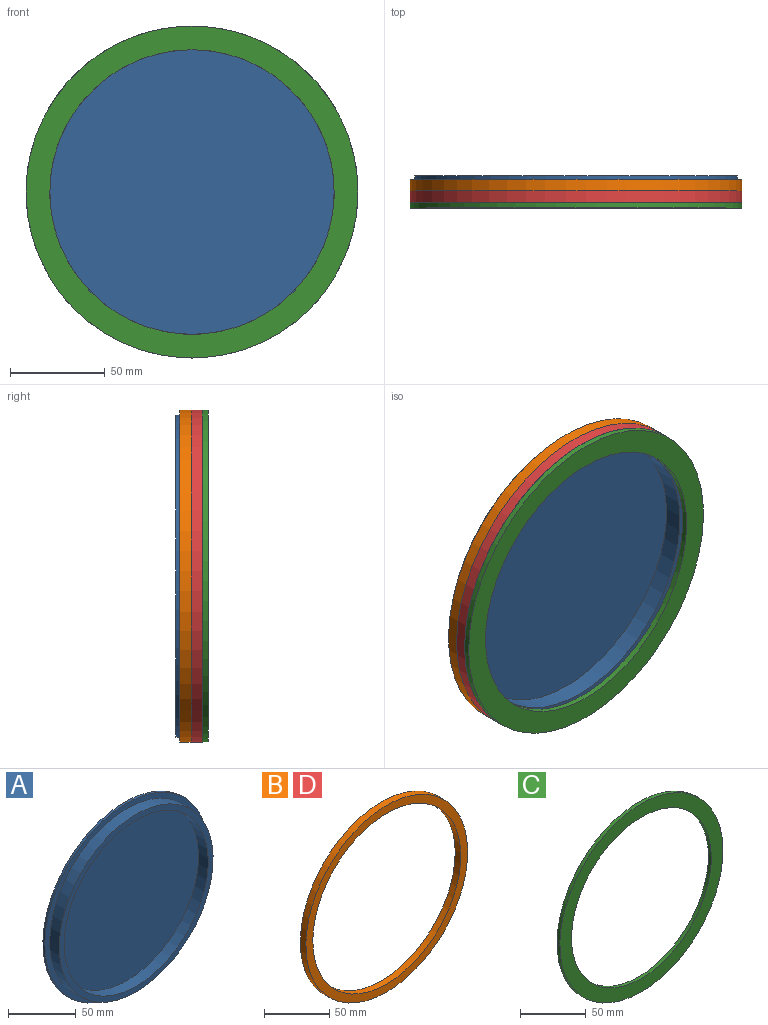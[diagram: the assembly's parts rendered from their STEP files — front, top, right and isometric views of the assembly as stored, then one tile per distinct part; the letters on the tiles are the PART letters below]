
ASSEMBLY  parts=4 mates=3
PART A: 7 faces, bbox 170x12x170 mm
  f0: cylinder r=75mm len=150mm, axis (0,1,0), area 4712.4mm2, adj f2,f6
  f1: cylinder r=80mm len=160mm, axis (0,1,0), area 5026.5mm2, adj f2,f3
  f2: plane 160x160mm, normal (0,-1,0), area 2434.7mm2, adj f0,f1
  f3: plane 170x170mm, normal (0,-1,0), area 2591.8mm2, adj f1,f4
  f4: cylinder r=85mm len=170mm, axis (0,1,0), area 1068.1mm2, adj f3,f5
  f5: plane 170x170mm, normal (0,1,0), area 22698mm2, adj f4
  f6: plane 150x150mm, normal (0,-1,0), area 17671.5mm2, adj f0
PART B: 4 faces, bbox 175x6x175 mm
  f0: cylinder r=80mm len=160mm, axis (0,1,0), area 3015.9mm2, adj f2,f3
  f1: cylinder r=87.5mm len=175mm, axis (0,1,0), area 3298.7mm2, adj f2,f3
  f2: plane 175x175mm, normal (0,-1,0), area 3946.6mm2, adj f0,f1
  f3: plane 175x175mm, normal (0,1,0), area 3946.6mm2, adj f0,f1
PART C: 4 faces, bbox 175x3x175 mm
  f0: cylinder r=75mm len=150mm, axis (0,1,0), area 1413.7mm2, adj f2,f3
  f1: cylinder r=87.5mm len=175mm, axis (0,1,0), area 1649.3mm2, adj f2,f3
  f2: plane 175x175mm, normal (0,-1,0), area 6381.4mm2, adj f0,f1
  f3: plane 175x175mm, normal (0,1,0), area 6381.4mm2, adj f0,f1
PART D: same geometry as B
PLACE A t=(-0.23,5.82,-0.07)mm fixed
PLACE B t=(-0.23,3.82,-0.07)mm
PLACE C rot(axis=(1,0,0),180deg) t=(-0.23,-11.18,-0.07)mm
PLACE D t=(-0.23,-2.18,-0.07)mm
MATE fastened A.f1 <-> B.f0  axis (0,-1,0) through (-0.23,3.82,-0.07)mm
MATE fastened D.f1 <-> C.f0  axis (0,-1,0) through (-0.23,-8.18,-0.07)mm
MATE fastened D.f1 <-> B.f0  axis (0,1,0) through (-0.23,-2.18,-0.07)mm
